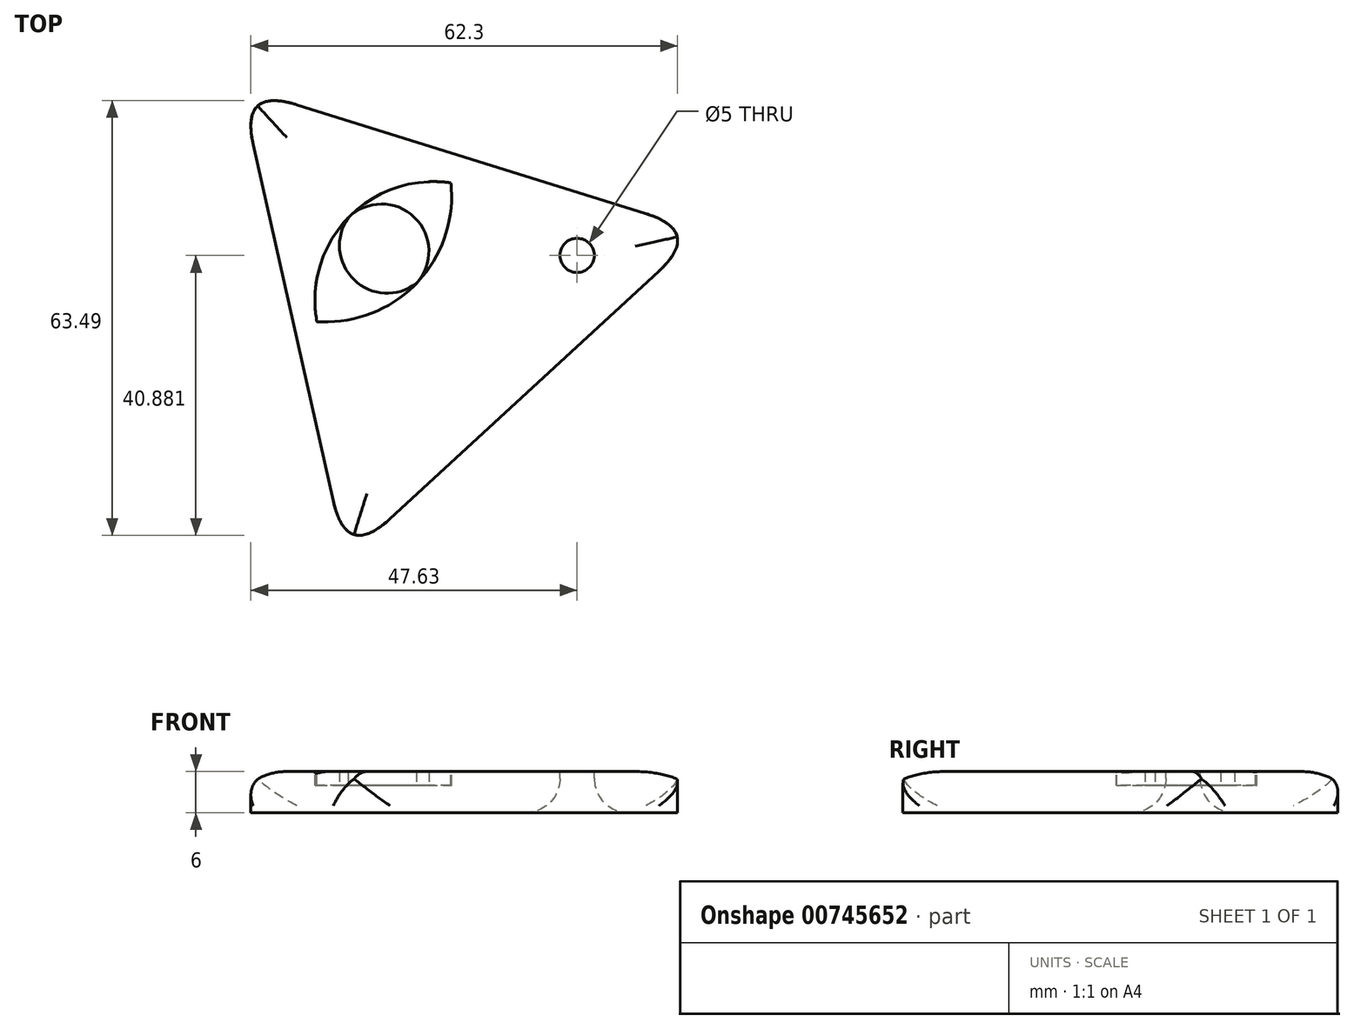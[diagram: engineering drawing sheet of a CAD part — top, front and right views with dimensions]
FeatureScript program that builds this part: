
annotation { "Feature Type Name" : "Feature", "Feature Type Description" : "" }
export const myFeature = defineFeature(function(context is Context, id is Id, definition is map)
    precondition{}
    {
        {
            var Q0;
            Q0=qCreatedBy(makeId("Top.planeOp"),FACE);
            var sketch = newSketch(context, id + "F0", { "sketchPlane" : qUnion([Q0])});
            skCircle(sketch, "E0.cCircle", {"center": v(0, 0) * mm, "radius": 20.4 * mm, "construction": true});
            skLineSegment(sketch, "E0.0", {"start": v(39.8, 8.94) * mm, "end": v(-12.15, -38.94) * mm});
            skLineSegment(sketch, "E0.1", {"start": v(-12.15, -38.94) * mm, "end": v(-27.64, 30) * mm});
            skLineSegment(sketch, "E0.2", {"start": v(-27.64, 30) * mm, "end": v(39.8, 8.94) * mm});
            skPoint(sketch, "E0.0.midPoint", {"position": v(13.82, -15) * mm});
            skSolve(sketch);
        }
        {
            var Q0;
            Q0=makeQuery(id+"F0.imprint","IMPRINT",FACE,{"disambiguationData":[TD([[makeQuery(id+"F0.imprint","IMPRINT",EDGE,{"derivedFrom":sQuery(id+"F0.wireOp",EDGE,"E0.0")}),-1.0]])]});
            extrude(context, id + "F1", {"entities" : qUnion([Q0]), "depth" : 6 * mm, "offsetDistance" : 25 * mm});
        }
        {
            var Q0;
            Q0=makeQuery(id+"F1.opExtrude","CAP_FACE",FACE,{"disambiguationData":[OSD([sQuery(id+"F0.wireOp",EDGE,"E0.0"),sQuery(id+"F0.wireOp",EDGE,"E0.1"),sQuery(id+"F0.wireOp",EDGE,"E0.2")])],"isStart":false});
            var sketch = newSketch(context, id + "F2", { "sketchPlane" : qUnion([Q0])});
            skArc(sketch, "E1", {"start": v(3.1, 16) * mm, "mid": v(-11.88, 10.9) * mm, "end": v(-16.46, -4.26) * mm});
            skArc(sketch, "E2", {"start": v(-16.46, -4.26) * mm, "mid": v(-1.95, 1.3) * mm, "end": v(3.1, 16) * mm});
            skSolve(sketch);
        }
        {
            var Q0;
            Q0=makeQuery(id+"F2.imprint","IMPRINT",FACE,{"disambiguationData":[TD([[makeQuery(id+"F2.imprint","IMPRINT",EDGE,{"derivedFrom":sQuery(id+"F2.wireOp",EDGE,"E1")}),1.0]])]});
            extrude(context, id + "F3", {"entities" : qUnion([Q0]), "operationType" : NewBodyOperationType.REMOVE, "oppositeDirection" : true, "depth" : 2 * mm, "offsetDistance" : 25 * mm});
        }
        {
            var Q0;
            Q0=makeQuery(id+"F3.boolean.opBoolean","COPY",FACE,{"derivedFrom":makeQuery(id+"F3.opExtrude","CAP_FACE",FACE,{"disambiguationData":[OSD([sQuery(id+"F2.wireOp",EDGE,"E1"),sQuery(id+"F2.wireOp",EDGE,"E2")])],"isStart":false})});
            var sketch = newSketch(context, id + "F4", { "sketchPlane" : qUnion([Q0])});
            skArc(sketch, "E3", {"start": v(-1.95, 1.3) * mm, "mid": v(-2.21, 10.98) * mm, "end": v(-11.88, 10.9) * mm});
            skArc(sketch, "E4", {"start": v(-11.88, 10.9) * mm, "mid": v(-11.03, 1.85) * mm, "end": v(-1.95, 1.3) * mm});
            skSolve(sketch);
        }
        {
            var Q0;
            Q0=makeQuery(id+"F4.imprint","IMPRINT",FACE,{"disambiguationData":[TD([[makeQuery(id+"F4.imprint","IMPRINT",EDGE,{"derivedFrom":sQuery(id+"F4.wireOp",EDGE,"E3")}),1.0]])]});
            extrude(context, id + "F5", {"entities" : qUnion([Q0]), "depth" : 2 * mm, "offsetDistance" : 25 * mm});
        }
        {
            var Q0;
            Q0=makeQuery(id+"F1.opExtrude","CAP_EDGE",EDGE,{"disambiguationData":[OSD([sQuery(id+"F0.wireOp",EDGE,"E0.1")])],"isStart":false});
            var Q1;
            Q1=makeQuery(id+"F1.opExtrude","CAP_EDGE",EDGE,{"disambiguationData":[OSD([sQuery(id+"F0.wireOp",EDGE,"E0.2")])],"isStart":false});
            var Q2;
            Q2=makeQuery(id+"F1.opExtrude","CAP_EDGE",EDGE,{"disambiguationData":[OSD([sQuery(id+"F0.wireOp",EDGE,"E0.0")])],"isStart":false});
            fillet(context, id + "F6", {"entities" : qUnion([Q0, Q1, Q2]), "radius" : 5 * mm, "tangentPropagation" : true, "allowEdgeOverflow" : false});
        }
        {
            var Q0;
            Q0=makeQuery(id+"F1.opExtrude","SWEPT_EDGE",EDGE,{"disambiguationData":[OSD([sQuery(id+"F0.wireOp",EDGE,"E0.1"),sQuery(id+"F0.wireOp",EDGE,"E0.2")])]});
            var Q1;
            Q1=makeQuery(id+"F1.opExtrude","SWEPT_EDGE",EDGE,{"disambiguationData":[OSD([sQuery(id+"F0.wireOp",EDGE,"E0.0"),sQuery(id+"F0.wireOp",EDGE,"E0.1")])]});
            var Q2;
            Q2=makeQuery(id+"F1.opExtrude","SWEPT_EDGE",EDGE,{"disambiguationData":[OSD([sQuery(id+"F0.wireOp",EDGE,"E0.0"),sQuery(id+"F0.wireOp",EDGE,"E0.2")])]});
            fillet(context, id + "F7", {"entities" : qUnion([Q0, Q1, Q2]), "radius" : 5 * mm, "rho" : 0.5, "crossSection" : FilletCrossSection.CONIC, "allowEdgeOverflow" : false});
        }
        {
            var Q0;
            Q0=makeQuery(id+"F6.opFillet","SPLIT",FACE,{"disambiguationData":[OD(0.0)],"derivedFrom":makeQuery(id+"F1.opExtrude","CAP_FACE",FACE,{"disambiguationData":[OSD([sQuery(id+"F0.wireOp",EDGE,"E0.0"),sQuery(id+"F0.wireOp",EDGE,"E0.1"),sQuery(id+"F0.wireOp",EDGE,"E0.2")])],"isStart":false})});
            var sketch = newSketch(context, id + "F8", { "sketchPlane" : qUnion([Q0])});
            skCircle(sketch, "E5", {"center": v(21.53, 5.41) * mm, "radius": 2.5 * mm});
            skSolve(sketch);
        }
        {
            var Q0;
            Q0=makeQuery(id+"F8.imprint","IMPRINT",FACE,{"disambiguationData":[TD([[makeQuery(id+"F8.imprint","IMPRINT",EDGE,{"derivedFrom":sQuery(id+"F8.wireOp",EDGE,"E5")}),1.0]])]});
            extrude(context, id + "F9", {"entities" : qUnion([Q0]), "operationType" : NewBodyOperationType.REMOVE, "oppositeDirection" : true, "depth" : 32.8 * mm, "offsetDistance" : 25 * mm});
        }
        {
            var Q0;
            Q0=makeQuery(id+"F9.boolean.opBoolean","COPY",EDGE,{"derivedFrom":makeQuery(id+"F9.opExtrude","CAP_EDGE",EDGE,{"disambiguationData":[OSD([sQuery(id+"F8.wireOp",EDGE,"E5")])],"isStart":true})});
            var Q1;
            Q1=makeQuery(id+"F9.boolean.opBoolean","INTERSECT",EDGE,{"derivedFrom":[makeQuery(id+"F1.opExtrude","CAP_FACE",FACE,{"disambiguationData":[OSD([sQuery(id+"F0.wireOp",EDGE,"E0.0"),sQuery(id+"F0.wireOp",EDGE,"E0.1"),sQuery(id+"F0.wireOp",EDGE,"E0.2")])],"isStart":true}),makeQuery(id+"F9.opExtrude","SWEPT_FACE",FACE,{"disambiguationData":[OSD([sQuery(id+"F8.wireOp",EDGE,"E5")])]})]});
            fillet(context, id + "F10", {"entities" : qUnion([Q0, Q1]), "radius" : 5 * mm, "tangentPropagation" : true, "allowEdgeOverflow" : false});
        }
    });
